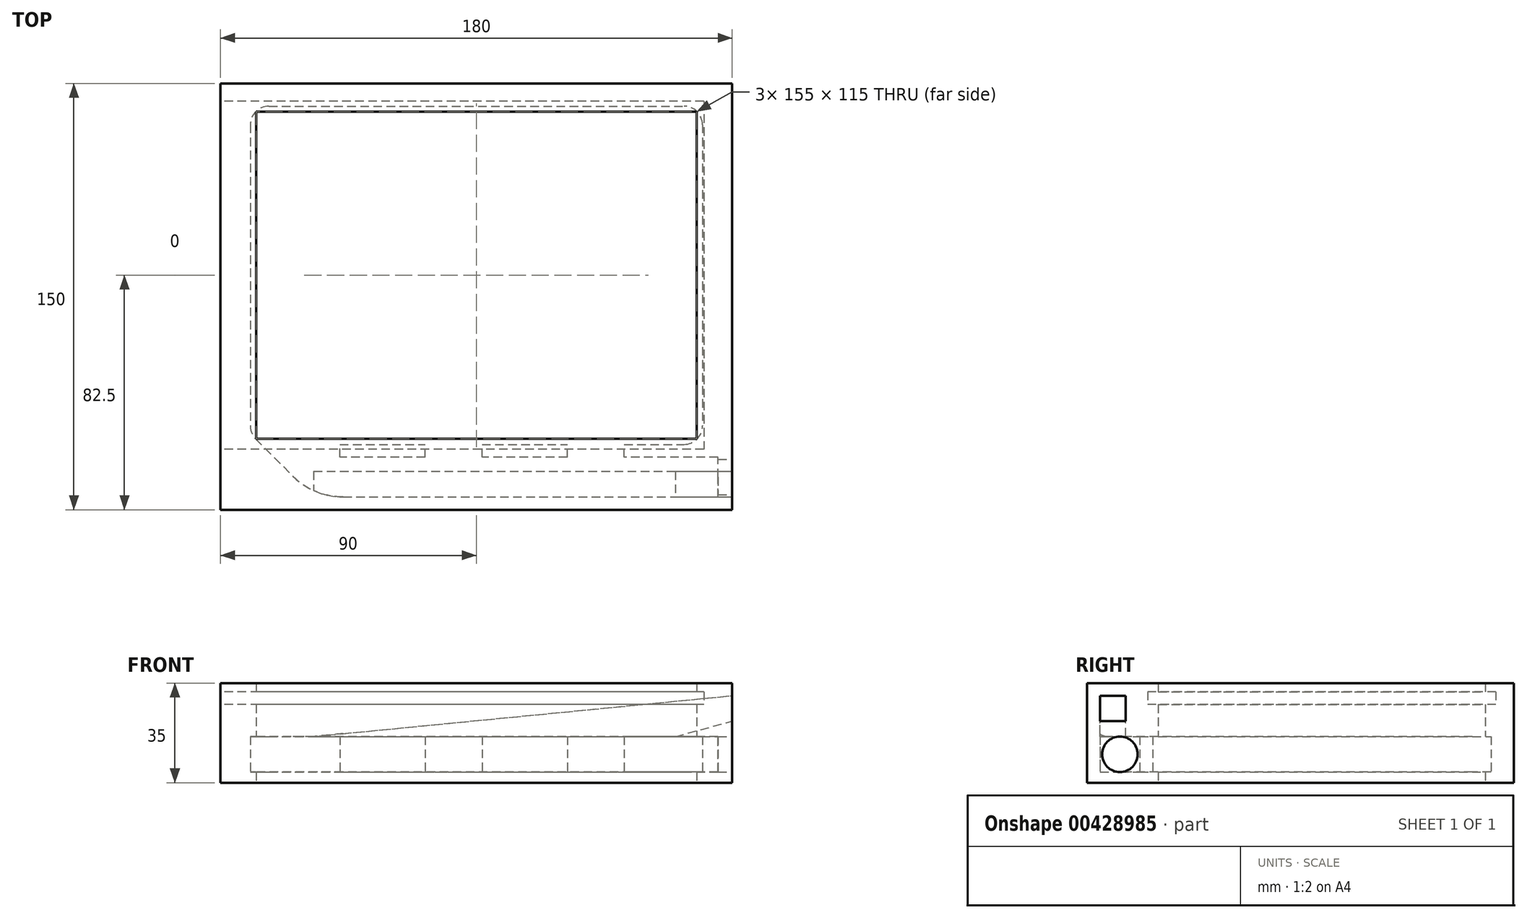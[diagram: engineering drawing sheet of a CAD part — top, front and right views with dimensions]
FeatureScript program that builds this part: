
annotation { "Feature Type Name" : "Feature", "Feature Type Description" : "" }
export const myFeature = defineFeature(function(context is Context, id is Id, definition is map)
    precondition{}
    {
        {
            var Q0;
            Q0=qCreatedBy(makeId("Top.planeOp"),FACE);
            var sketch = newSketch(context, id + "F0", { "sketchPlane" : qUnion([Q0])});
            skLineSegment(sketch, "E0.bottom", {"start": v(0, 0) * mm, "end": v(180, 0) * mm});
            skLineSegment(sketch, "E0.top", {"start": v(0, 150) * mm, "end": v(180, 150) * mm});
            skLineSegment(sketch, "E0.left", {"start": v(0, 0) * mm, "end": v(0, 150) * mm});
            skLineSegment(sketch, "E0.right", {"start": v(180, 0) * mm, "end": v(180, 150) * mm});
            skLineSegment(sketch, "E1.bottom", {"start": v(12.5, 140) * mm, "end": v(167.5, 140) * mm});
            skLineSegment(sketch, "E1.top", {"start": v(12.5, 25) * mm, "end": v(167.5, 25) * mm});
            skLineSegment(sketch, "E1.left", {"start": v(12.5, 140) * mm, "end": v(12.5, 25) * mm});
            skLineSegment(sketch, "E1.right", {"start": v(167.5, 140) * mm, "end": v(167.5, 25) * mm});
            skSolve(sketch);
        }
        {
            var Q0;
            Q0 = qSketchRegion(id + "F0", true);
            extrude(context, id + "F1", {"entities" : qUnion([Q0]), "depth" : 35 * mm});
        }
        {
            var Q0;
            Q0=makeQuery(id+"F1.opExtrude","SWEPT_FACE",FACE,{"disambiguationData":[OSD([sQuery(id+"F0.wireOp",EDGE,"E0.left")])]});
            var sketch = newSketch(context, id + "F2", { "sketchPlane" : qUnion([Q0])});
            skLineSegment(sketch, "E2.0.1", {"start": v(-140, 0) * mm, "end": v(-140, 35) * mm, "construction": true});
            skLineSegment(sketch, "E2.0.3", {"start": v(-140, 35) * mm, "end": v(-140, 0) * mm, "construction": true});
            skLineSegment(sketch, "E3.0.1", {"start": v(-25, 0) * mm, "end": v(-25, 35) * mm, "construction": true});
            skLineSegment(sketch, "E3.0.3", {"start": v(-25, 35) * mm, "end": v(-25, 0) * mm, "construction": true});
            skLineSegment(sketch, "E4.bottom", {"start": v(-143.75, 32) * mm, "end": v(-21.25, 32) * mm});
            skLineSegment(sketch, "E4.top", {"start": v(-143.75, 27.5) * mm, "end": v(-21.25, 27.5) * mm});
            skLineSegment(sketch, "E4.left", {"start": v(-143.75, 32) * mm, "end": v(-143.75, 27.5) * mm});
            skLineSegment(sketch, "E4.right", {"start": v(-21.25, 32) * mm, "end": v(-21.25, 27.5) * mm});
            skSolve(sketch);
        }
        {
            var Q0;
            Q0 = qSketchRegion(id + "F2", true);
            extrude(context, id + "F3", {"entities" : qUnion([Q0]), "operationType" : NewBodyOperationType.REMOVE, "oppositeDirection" : true, "depth" : 170 * mm});
        }
        {
            var Q0;
            Q0=makeQuery(id+"F1.opExtrude","CAP_FACE",FACE,{"disambiguationData":[OSD([sQuery(id+"F0.wireOp",EDGE,"E0.bottom"),sQuery(id+"F0.wireOp",EDGE,"E0.top"),sQuery(id+"F0.wireOp",EDGE,"E0.left"),sQuery(id+"F0.wireOp",EDGE,"E0.right"),sQuery(id+"F0.wireOp",EDGE,"E1.bottom"),sQuery(id+"F0.wireOp",EDGE,"E1.top"),sQuery(id+"F0.wireOp",EDGE,"E1.left"),sQuery(id+"F0.wireOp",EDGE,"E1.right")])],"isStart":true});
            cPlane(context, id + "F4", {"entities" : qUnion([Q0]), "cplaneType" : CPlaneType.OFFSET, "offset" : 10 * mm, "oppositeDirection" : true, "width" : 150 * mm, "height" : 150 * mm});
        }
        {
            var Q0;
            Q0=qCreatedBy(id+"F4.planeOp",FACE);
            var sketch = newSketch(context, id + "F5", { "sketchPlane" : qUnion([Q0])});
            skLineSegment(sketch, "E5.bottom", {"start": v(10.5, -142) * mm, "end": v(169.5, -142) * mm});
            skLineSegment(sketch, "E5.top", {"start": v(10.5, -23) * mm, "end": v(169.5, -23) * mm});
            skLineSegment(sketch, "E5.left", {"start": v(10.5, -142) * mm, "end": v(10.5, -23) * mm});
            skLineSegment(sketch, "E5.right", {"start": v(169.5, -142) * mm, "end": v(169.5, -23) * mm});
            skSolve(sketch);
        }
        {
            var Q0;
            Q0 = qSketchRegion(id + "F5", true);
            extrude(context, id + "F6", {"entities" : qUnion([Q0]), "operationType" : NewBodyOperationType.REMOVE, "endBound" : BoundingType.SYMMETRIC, "oppositeDirection" : true, "depth" : 12.5 * mm});
        }
        {
            var Q0;
            Q0=makeQuery(id+"F6.boolean.opBoolean","COPY",EDGE,{"derivedFrom":makeQuery(id+"F6.opExtrude","SWEPT_EDGE",EDGE,{"disambiguationData":[OSD([sQuery(id+"F5.wireOp",EDGE,"E5.bottom"),sQuery(id+"F5.wireOp",EDGE,"E5.right")])]})});
            var Q1;
            Q1=makeQuery(id+"F6.boolean.opBoolean","COPY",EDGE,{"derivedFrom":makeQuery(id+"F6.opExtrude","SWEPT_EDGE",EDGE,{"disambiguationData":[OSD([sQuery(id+"F5.wireOp",EDGE,"E5.bottom"),sQuery(id+"F5.wireOp",EDGE,"E5.left")])]})});
            var Q2;
            Q2=makeQuery(id+"F6.boolean.opBoolean","COPY",EDGE,{"derivedFrom":makeQuery(id+"F6.opExtrude","SWEPT_EDGE",EDGE,{"disambiguationData":[OSD([sQuery(id+"F5.wireOp",EDGE,"E5.top"),sQuery(id+"F5.wireOp",EDGE,"E5.left")])]})});
            var Q3;
            Q3=makeQuery(id+"F6.boolean.opBoolean","COPY",EDGE,{"derivedFrom":makeQuery(id+"F6.opExtrude","SWEPT_EDGE",EDGE,{"disambiguationData":[OSD([sQuery(id+"F5.wireOp",EDGE,"E5.top"),sQuery(id+"F5.wireOp",EDGE,"E5.right")])]})});
            fillet(context, id + "F7", {"entities" : qUnion([Q0, Q1, Q2, Q3]), "radius" : 6.5 * mm, "tangentPropagation" : true, "allowEdgeOverflow" : false});
        }
        {
            var Q0;
            Q0=qCreatedBy(id+"F4.planeOp",FACE);
            var sketch = newSketch(context, id + "F8", { "sketchPlane" : qUnion([Q0])});
            skLineSegment(sketch, "E6.0.0", {"start": v(163, -23) * mm, "end": v(17, -23) * mm, "construction": true});
            skLineSegment(sketch, "E6.0.2", {"start": v(17, -23) * mm, "end": v(163, -23) * mm, "construction": true});
            skArc(sketch, "E7.0.0", {"start": v(10.5, -29.5) * mm, "mid": v(12.4, -24.9) * mm, "end": v(17, -23) * mm, "construction": true});
            skArc(sketch, "E7.0.2", {"start": v(12.4, -24.9) * mm, "mid": v(14.51, -23.5) * mm, "end": v(17, -23) * mm, "construction": true});
            skLineSegment(sketch, "E8.0.0", {"start": v(10.5, -135.5) * mm, "end": v(10.5, -29.5) * mm, "construction": true});
            skLineSegment(sketch, "E8.0.2", {"start": v(10.5, -29.5) * mm, "end": v(10.5, -135.5) * mm, "construction": true});
            skLineSegment(sketch, "E9", {"start": v(12.4, -24.9) * mm, "end": v(32.8, -4.5) * mm});
            skLineSegment(sketch, "E10.0", {"start": v(180, 0) * mm, "end": v(180, -150) * mm, "construction": true});
            skLineSegment(sketch, "E11", {"start": v(32.8, -4.5) * mm, "end": v(180, -4.5) * mm});
            skLineSegment(sketch, "E12", {"start": v(180, -4.5) * mm, "end": v(180, -18.5) * mm});
            skLineSegment(sketch, "E13", {"start": v(180, -18.5) * mm, "end": v(42, -18.5) * mm});
            skLineSegment(sketch, "E14", {"start": v(42, -18.5) * mm, "end": v(42, -23) * mm});
            skLineSegment(sketch, "E15", {"start": v(42, -23) * mm, "end": v(17, -23) * mm});
            skArc(sketch, "E16.0.0", {"start": v(10.5, -29.5) * mm, "mid": v(12.4, -24.9) * mm, "end": v(17, -23) * mm});
            skArc(sketch, "E16.0.2", {"start": v(10.5, -29.5) * mm, "mid": v(12.4, -24.9) * mm, "end": v(17, -23) * mm});
            skSolve(sketch);
        }
        {
            var Q0;
            Q0 = qSketchRegion(id + "F8", true);
            extrude(context, id + "F9", {"entities" : qUnion([Q0]), "operationType" : NewBodyOperationType.REMOVE, "endBound" : BoundingType.SYMMETRIC, "oppositeDirection" : true, "depth" : 12.5 * mm});
        }
        {
            var Q0;
            Q0=makeQuery(id+"F9.boolean.opBoolean","COPY",FACE,{"derivedFrom":makeQuery(id+"F9.opExtrude","SWEPT_FACE",FACE,{"disambiguationData":[OSD([sQuery(id+"F8.wireOp",EDGE,"E11")])]})});
            var sketch = newSketch(context, id + "F10", { "sketchPlane" : qUnion([Q0])});
            skLineSegment(sketch, "E17.0", {"start": v(-32.8, 16.25) * mm, "end": v(-125.23, 16.25) * mm, "construction": true});
            skLineSegment(sketch, "E18.0", {"start": v(-32.8, 3.75) * mm, "end": v(-180, 3.75) * mm, "construction": true});
            skLineSegment(sketch, "E19.0", {"start": v(-180, 35) * mm, "end": v(-180, 0) * mm, "construction": true});
            skLineSegment(sketch, "E20", {"start": v(-125.23, 16.25) * mm, "end": v(-160, 16.25) * mm});
            skLineSegment(sketch, "E21", {"start": v(-160, 16.25) * mm, "end": v(-180, 21.6) * mm});
            skLineSegment(sketch, "E22", {"start": v(-180, 21.6) * mm, "end": v(-180, 30.6) * mm});
            skLineSegment(sketch, "E23", {"start": v(-32.8, 16.25) * mm, "end": v(-180, 30.6) * mm});
            skLineSegment(sketch, "E24.trimOffspring", {"start": v(-160, 16.25) * mm, "end": v(-180, 16.25) * mm, "construction": true});
            skLineSegment(sketch, "E25", {"start": v(-32.8, 16.25) * mm, "end": v(-160, 16.25) * mm});
            skSolve(sketch);
        }
        {
            var Q0;
            Q0 = qSketchRegion(id + "F10", true);
            var Q1;
            Q1=makeQuery(id+"F9.boolean.opBoolean","COPY",FACE,{"derivedFrom":makeQuery(id+"F9.opExtrude","SWEPT_FACE",FACE,{"disambiguationData":[OSD([sQuery(id+"F8.wireOp",EDGE,"E13")])]})});
            extrude(context, id + "F11", {"entities" : qUnion([Q0]), "operationType" : NewBodyOperationType.REMOVE, "endBoundEntityFace" : qUnion([Q1]), "depth" : 9 * mm});
        }
        {
            var Q0;
            Q0=makeQuery(id+"F9.boolean.opBoolean","COPY",EDGE,{"derivedFrom":makeQuery(id+"F9.opExtrude","SWEPT_EDGE",EDGE,{"disambiguationData":[OSD([sQuery(id+"F8.wireOp",EDGE,"E9"),sQuery(id+"F8.wireOp",EDGE,"E11")])]})});
            fillet(context, id + "F12", {"entities" : qUnion([Q0]), "radius" : 25 * mm, "tangentPropagation" : true, "allowEdgeOverflow" : false});
        }
        {
            var Q0;
            Q0=makeQuery(id+"F1.opExtrude","SWEPT_FACE",FACE,{"disambiguationData":[OSD([sQuery(id+"F0.wireOp",EDGE,"E0.right")])]});
            var sketch = newSketch(context, id + "F13", { "sketchPlane" : qUnion([Q0])});
            skCircle(sketch, "E26", {"center": v(11.5, 10) * mm, "radius": 6.25 * mm});
            skPoint(sketch, "E26.centerSnap0", {"position": v(18.5, 10) * mm});
            skPoint(sketch, "E26.centerSnap1", {"position": v(11.5, 16.25) * mm});
            skLineSegment(sketch, "E27.0", {"start": v(4.5, 16.25) * mm, "end": v(18.5, 16.25) * mm});
            skLineSegment(sketch, "E28.0", {"start": v(18.5, 16.25) * mm, "end": v(18.5, 3.75) * mm});
            skLineSegment(sketch, "E29.0", {"start": v(4.5, 3.75) * mm, "end": v(18.5, 3.75) * mm});
            skLineSegment(sketch, "E30.0", {"start": v(4.5, 16.25) * mm, "end": v(4.5, 3.75) * mm});
            skSolve(sketch);
        }
        {
            var Q0;
            {var subQ5=sQuery(id+"F13.wireOp",EDGE,"E28.0");Q0=makeQuery(id+"F13.imprint","IMPRINT",FACE,{"disambiguationData":[TD([[makeQuery(id+"F13.imprint","IMPRINT",EDGE,{"derivedFrom":subQ5}),-1.0]])]});}
            var Q1;
            {var subQ5=sQuery(id+"F13.wireOp",EDGE,"E30.0");Q1=makeQuery(id+"F13.imprint","IMPRINT",FACE,{"disambiguationData":[TD([[makeQuery(id+"F13.imprint","IMPRINT",EDGE,{"derivedFrom":subQ5}),1.0]])]});}
            extrude(context, id + "F14", {"entities" : qUnion([Q0, Q1]), "operationType" : NewBodyOperationType.ADD, "oppositeDirection" : true, "depth" : 5 * mm});
        }
        {
            var Q0;
            Q0=makeQuery(id+"F6.boolean.opBoolean","COPY",FACE,{"derivedFrom":makeQuery(id+"F6.opExtrude","SWEPT_FACE",FACE,{"disambiguationData":[OSD([sQuery(id+"F5.wireOp",EDGE,"E5.top")])]})});
            var sketch = newSketch(context, id + "F15", { "sketchPlane" : qUnion([Q0])});
            skLineSegment(sketch, "E31.bottom", {"start": v(-142, 16.25) * mm, "end": v(-122, 16.25) * mm});
            skLineSegment(sketch, "E31.top", {"start": v(-142, 3.75) * mm, "end": v(-122, 3.75) * mm});
            skLineSegment(sketch, "E31.left", {"start": v(-142, 16.25) * mm, "end": v(-142, 3.75) * mm});
            skLineSegment(sketch, "E31.right", {"start": v(-122, 16.25) * mm, "end": v(-122, 3.75) * mm});
            skLineSegment(sketch, "E32.bottom", {"start": v(-92, 16.25) * mm, "end": v(-72, 16.25) * mm});
            skLineSegment(sketch, "E32.top", {"start": v(-92, 3.75) * mm, "end": v(-72, 3.75) * mm});
            skLineSegment(sketch, "E32.left", {"start": v(-92, 16.25) * mm, "end": v(-92, 3.75) * mm});
            skLineSegment(sketch, "E32.right", {"start": v(-72, 16.25) * mm, "end": v(-72, 3.75) * mm});
            skSolve(sketch);
        }
        {
            var Q0;
            Q0 = qSketchRegion(id + "F15", true);
            extrude(context, id + "F16", {"entities" : qUnion([Q0]), "operationType" : NewBodyOperationType.REMOVE, "endBound" : BoundingType.UP_TO_NEXT, "oppositeDirection" : true, "depth" : 25 * mm});
        }
    });
